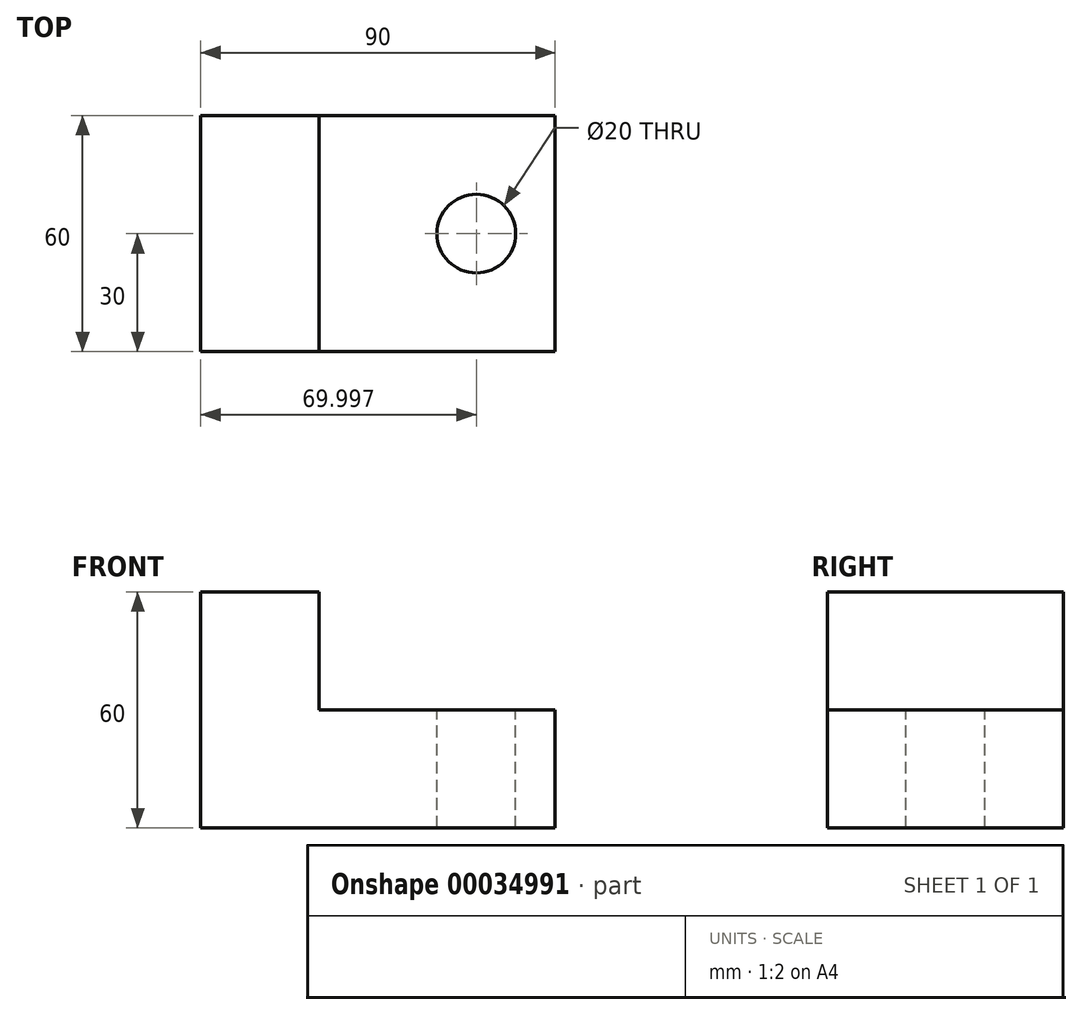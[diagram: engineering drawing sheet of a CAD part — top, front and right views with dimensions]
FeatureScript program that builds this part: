
annotation { "Feature Type Name" : "Feature", "Feature Type Description" : "" }
export const myFeature = defineFeature(function(context is Context, id is Id, definition is map)
    precondition{}
    {
        {
            var Q0;
            Q0=qCreatedBy(makeId("Front.planeOp"),FACE);
            var sketch = newSketch(context, id + "F0", { "sketchPlane" : qUnion([Q0])});
            skLineSegment(sketch, "E0.bottom", {"start": v(-51.02, 26.91) * mm, "end": v(38.98, 26.91) * mm});
            skLineSegment(sketch, "E0.top", {"start": v(-51.02, -33.09) * mm, "end": v(38.98, -33.09) * mm});
            skLineSegment(sketch, "E0.left", {"start": v(-51.02, 26.91) * mm, "end": v(-51.02, -33.09) * mm});
            skLineSegment(sketch, "E0.right", {"start": v(38.98, 26.91) * mm, "end": v(38.98, -33.09) * mm});
            skSolve(sketch);
        }
        {
            var Q0;
            Q0=makeQuery(id+"F0.imprint","IMPRINT",FACE,{"disambiguationData":[TD([[makeQuery(id+"F0.imprint","IMPRINT",EDGE,{"derivedFrom":sQuery(id+"F0.wireOp",EDGE,"E0.bottom")}),-1.0]])]});
            extrude(context, id + "F1", {"entities" : qUnion([Q0]), "depth" : 60 * mm});
        }
        {
            var Q0;
            Q0=makeQuery(id+"F1.opExtrude","CAP_FACE",FACE,{"disambiguationData":[OSD([sQuery(id+"F0.wireOp",EDGE,"E0.bottom"),sQuery(id+"F0.wireOp",EDGE,"E0.top"),sQuery(id+"F0.wireOp",EDGE,"E0.left"),sQuery(id+"F0.wireOp",EDGE,"E0.right")])],"isStart":false});
            var sketch = newSketch(context, id + "F2", { "sketchPlane" : qUnion([Q0])});
            skSolve(sketch);
        }
        {
            var Q0;
            Q0=makeQuery(id+"F2.imprint","IMPRINT",FACE,{"disambiguationData":[TD([[makeQuery(id+"F2.imprint","IMPRINT",EDGE,{"derivedFrom":makeQuery(id+"F1.opExtrude","CAP_EDGE",EDGE,{"disambiguationData":[OSD([sQuery(id+"F0.wireOp",EDGE,"E0.bottom")])],"isStart":false})}),-1.0]])]});
            var sketch = newSketch(context, id + "F3", { "sketchPlane" : qUnion([Q0])});
            skLineSegment(sketch, "E1.bottom", {"start": v(-21.02, 26.91) * mm, "end": v(38.98, 26.91) * mm});
            skLineSegment(sketch, "E1.top", {"start": v(-21.02, -3.09) * mm, "end": v(38.98, -3.09) * mm});
            skLineSegment(sketch, "E1.left", {"start": v(-21.02, 26.91) * mm, "end": v(-21.02, -3.09) * mm});
            skLineSegment(sketch, "E1.right", {"start": v(38.98, 26.91) * mm, "end": v(38.98, -3.09) * mm});
            skSolve(sketch);
        }
        {
            var Q0;
            Q0=makeQuery(id+"F3.imprint","IMPRINT",FACE,{"disambiguationData":[TD([[makeQuery(id+"F3.imprint","IMPRINT",EDGE,{"derivedFrom":sQuery(id+"F3.wireOp",EDGE,"E1.bottom")}),-1.0]])]});
            extrude(context, id + "F4", {"entities" : qUnion([Q0]), "operationType" : NewBodyOperationType.REMOVE, "oppositeDirection" : true, "depth" : 60 * mm});
        }
        {
            var Q0;
            Q0=makeQuery(id+"F4.boolean.opBoolean","COPY",FACE,{"derivedFrom":makeQuery(id+"F4.opExtrude","SWEPT_FACE",FACE,{"disambiguationData":[OSD([sQuery(id+"F3.wireOp",EDGE,"E1.top")])]})});
            var sketch = newSketch(context, id + "F5", { "sketchPlane" : qUnion([Q0])});
            skCircle(sketch, "E2", {"center": v(18.98, -30) * mm, "radius": 10 * mm});
            skSolve(sketch);
        }
        {
            var Q0;
            Q0=makeQuery(id+"F5.imprint","IMPRINT",FACE,{"disambiguationData":[TD([[makeQuery(id+"F5.imprint","IMPRINT",EDGE,{"derivedFrom":sQuery(id+"F5.wireOp",EDGE,"E2")}),1.0]])]});
            extrude(context, id + "F6", {"entities" : qUnion([Q0]), "operationType" : NewBodyOperationType.REMOVE, "oppositeDirection" : true, "depth" : 57.47 * mm});
        }
    });
